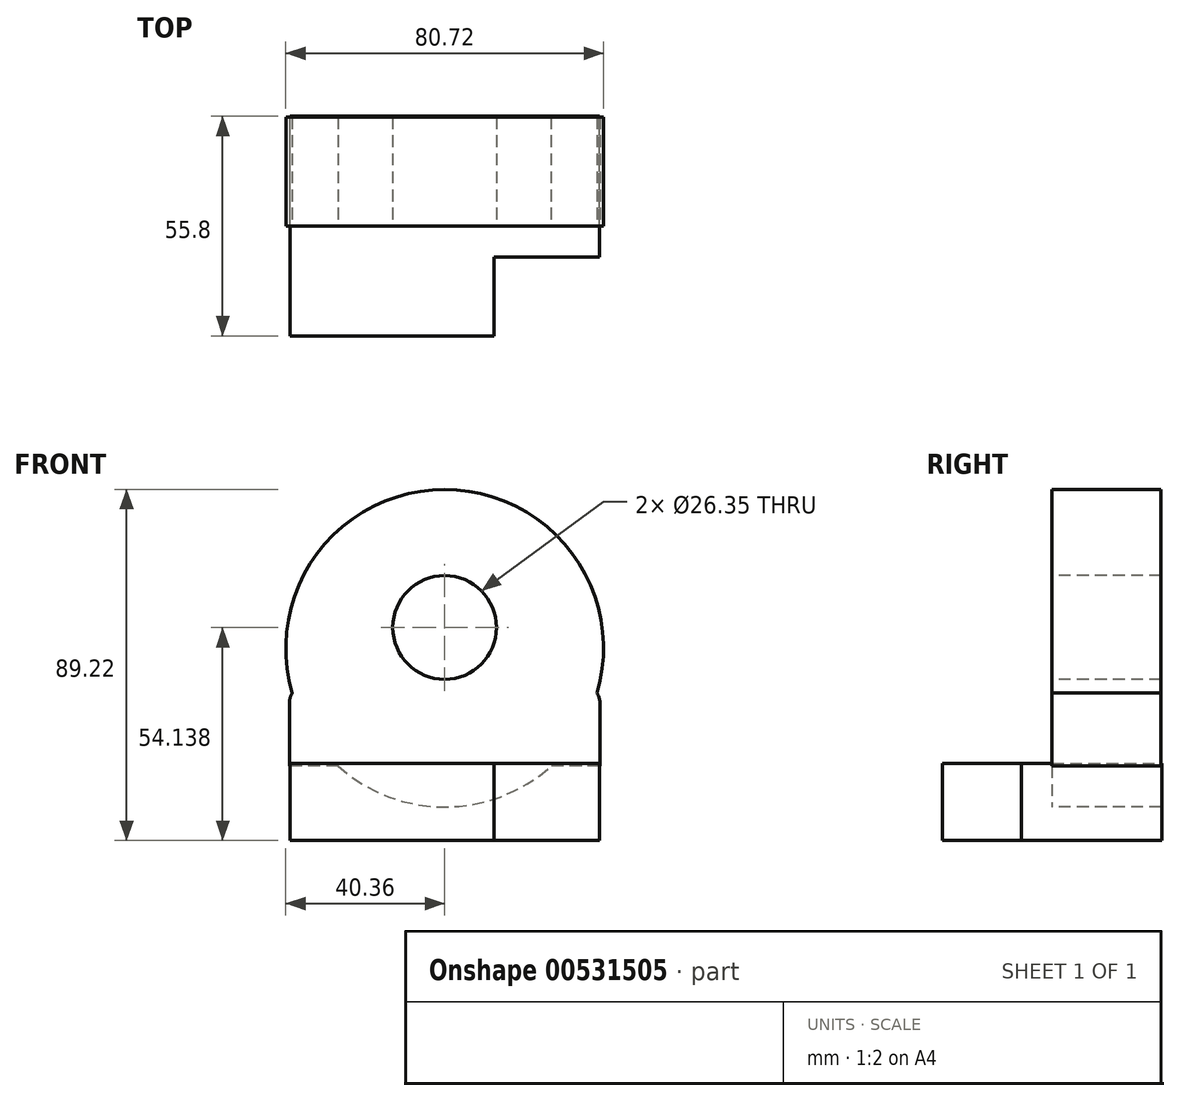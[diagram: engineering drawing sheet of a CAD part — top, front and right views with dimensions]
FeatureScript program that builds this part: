
annotation { "Feature Type Name" : "Feature", "Feature Type Description" : "" }
export const myFeature = defineFeature(function(context is Context, id is Id, definition is map)
    precondition{}
    {
        {
            var Q0;
            Q0=qCreatedBy(makeId("Top.planeOp"),FACE);
            var sketch = newSketch(context, id + "F0", { "sketchPlane" : qUnion([Q0])});
            skLineSegment(sketch, "E0.bottom", {"start": v(-39.31, -27.9) * mm, "end": v(39.31, -27.9) * mm});
            skLineSegment(sketch, "E0.top", {"start": v(-39.31, 27.9) * mm, "end": v(39.31, 27.9) * mm});
            skLineSegment(sketch, "E0.left", {"start": v(-39.31, -27.9) * mm, "end": v(-39.31, 27.9) * mm});
            skLineSegment(sketch, "E0.right", {"start": v(39.31, -27.9) * mm, "end": v(39.31, 27.9) * mm});
            skPoint(sketch, "E0.middle", {"position": v(0, 0) * mm});
            skSolve(sketch);
        }
        {
            var Q0;
            Q0=makeQuery(id+"F0.imprint","IMPRINT",FACE,{"disambiguationData":[TD([[makeQuery(id+"F0.imprint","IMPRINT",EDGE,{"derivedFrom":sQuery(id+"F0.wireOp",EDGE,"E0.bottom")}),1.0]])]});
            extrude(context, id + "F1", {"entities" : qUnion([Q0]), "depth" : 19.56 * mm, "offsetDistance" : 25.4 * mm});
        }
        {
            var Q0;
            Q0=qCreatedBy(makeId("Top.planeOp"),FACE);
            var sketch = newSketch(context, id + "F2", { "sketchPlane" : qUnion([Q0])});
            skLineSegment(sketch, "E1.bottom", {"start": v(39.62, -28.21) * mm, "end": v(12.49, -28.21) * mm});
            skLineSegment(sketch, "E1.top", {"start": v(39.62, -7.86) * mm, "end": v(12.49, -7.86) * mm});
            skLineSegment(sketch, "E1.left", {"start": v(39.62, -28.21) * mm, "end": v(39.62, -7.86) * mm});
            skLineSegment(sketch, "E1.right", {"start": v(12.49, -28.21) * mm, "end": v(12.49, -7.86) * mm});
            skPoint(sketch, "E1.middle", {"position": v(26.05, -18.04) * mm});
            skSolve(sketch);
        }
        {
            var Q0;
            Q0=makeQuery(id+"F2.imprint","IMPRINT",FACE,{"disambiguationData":[TD([[makeQuery(id+"F2.imprint","IMPRINT",EDGE,{"derivedFrom":sQuery(id+"F2.wireOp",EDGE,"E1.bottom")}),-1.0]])]});
            extrude(context, id + "F3", {"entities" : qUnion([Q0]), "operationType" : NewBodyOperationType.REMOVE, "depth" : 29.2 * mm, "offsetDistance" : 25.4 * mm});
        }
        {
            var Q0;
            Q0=qCreatedBy(makeId("Front.planeOp"),FACE);
            var sketch = newSketch(context, id + "F4", { "sketchPlane" : qUnion([Q0])});
            skCircle(sketch, "E2", {"center": v(0, 48.87) * mm, "radius": 40.36 * mm});
            skLineSegment(sketch, "E3.bottom", {"start": v(39.45, 18.93) * mm, "end": v(-39.45, 18.93) * mm});
            skLineSegment(sketch, "E3.top", {"start": v(39.45, 37.47) * mm, "end": v(-39.45, 37.47) * mm});
            skLineSegment(sketch, "E3.left", {"start": v(39.45, 18.93) * mm, "end": v(39.45, 37.47) * mm});
            skLineSegment(sketch, "E3.right", {"start": v(-39.45, 18.93) * mm, "end": v(-39.45, 37.47) * mm});
            skPoint(sketch, "E3.middle", {"position": v(0, 28.2) * mm});
            skSolve(sketch);
        }
        {
            var Q0;
            {var subQ5=sQuery(id+"F4.wireOp",EDGE,"E3.right");Q0=makeQuery(id+"F4.imprint","IMPRINT",FACE,{"disambiguationData":[TD([[makeQuery(id+"F4.imprint","IMPRINT",EDGE,{"derivedFrom":subQ5}),-1.0]])]});}
            var Q1;
            {var subQ0=sQuery(id+"F4.wireOp",EDGE,"E3.bottom");var subQ1=sQuery(id+"F4.wireOp",EDGE,"E2");var subQ2=makeQuery(id+"F4.imprint","INTERSECT",VERTEX,{"disambiguationData":[OD(0.0)],"derivedFrom":[subQ1,subQ0]});Q1=makeQuery(id+"F4.imprint","IMPRINT",FACE,{"disambiguationData":[TD([[makeQuery(id+"F4.imprint","IMPRINT",EDGE,{"disambiguationData":[TD([[subQ2,1.0]])],"derivedFrom":subQ1}),1.0]])]});}
            var Q2;
            {var subQ0=sQuery(id+"F4.wireOp",EDGE,"E3.top");var subQ1=sQuery(id+"F4.wireOp",EDGE,"E2");var subQ2=makeQuery(id+"F4.imprint","INTERSECT",VERTEX,{"disambiguationData":[OD(0.0)],"derivedFrom":[subQ1,subQ0]});Q2=makeQuery(id+"F4.imprint","IMPRINT",FACE,{"disambiguationData":[TD([[makeQuery(id+"F4.imprint","IMPRINT",EDGE,{"disambiguationData":[TD([[subQ2,1.0]])],"derivedFrom":subQ1}),1.0]])]});}
            var Q3;
            {var subQ5=sQuery(id+"F4.wireOp",EDGE,"E3.left");Q3=makeQuery(id+"F4.imprint","IMPRINT",FACE,{"disambiguationData":[TD([[makeQuery(id+"F4.imprint","IMPRINT",EDGE,{"derivedFrom":subQ5}),1.0]])]});}
            var Q4;
            {var subQ0=sQuery(id+"F4.wireOp",EDGE,"E3.top");var subQ1=sQuery(id+"F4.wireOp",EDGE,"E2");var subQ2=makeQuery(id+"F4.imprint","INTERSECT",VERTEX,{"disambiguationData":[OD(0.0)],"derivedFrom":[subQ1,subQ0]});Q4=makeQuery(id+"F4.imprint","IMPRINT",FACE,{"disambiguationData":[TD([[makeQuery(id+"F4.imprint","IMPRINT",EDGE,{"disambiguationData":[TD([[subQ2,-1.0]])],"derivedFrom":subQ1}),1.0]])]});}
            extrude(context, id + "F5", {"entities" : qUnion([Q0, Q1, Q2, Q3, Q4]), "oppositeDirection" : true, "depth" : 27.7 * mm, "offsetDistance" : 25.4 * mm});
        }
        {
            var Q0;
            Q0=makeQuery(id+"F5.opExtrude","CAP_FACE",FACE,{"disambiguationData":[OSD([sQuery(id+"F4.wireOp",EDGE,"E2"),sQuery(id+"F4.wireOp",EDGE,"E3.bottom"),sQuery(id+"F4.wireOp",EDGE,"E3.top"),sQuery(id+"F4.wireOp",EDGE,"E3.left"),sQuery(id+"F4.wireOp",EDGE,"E3.right")])],"isStart":true});
            var sketch = newSketch(context, id + "F6", { "sketchPlane" : qUnion([Q0])});
            skCircle(sketch, "E4", {"center": v(0, 54.14) * mm, "radius": 13.18 * mm});
            skSolve(sketch);
        }
        {
            var Q0;
            Q0=makeQuery(id+"F6.imprint","IMPRINT",FACE,{"disambiguationData":[TD([[makeQuery(id+"F6.imprint","IMPRINT",EDGE,{"derivedFrom":sQuery(id+"F6.wireOp",EDGE,"E4")}),1.0]])]});
            extrude(context, id + "F7", {"entities" : qUnion([Q0]), "operationType" : NewBodyOperationType.REMOVE, "oppositeDirection" : true, "depth" : 29.2 * mm, "offsetDistance" : 25.4 * mm});
        }
        {
            var Q0;
            Q0=makeQuery(id+"F5.opExtrude","SWEPT_EDGE",EDGE,{"disambiguationData":[OSD([sQuery(id+"F4.wireOp",EDGE,"E3.top"),sQuery(id+"F4.wireOp",EDGE,"E3.right")])]});
            var Q1;
            Q1=makeQuery(id+"F5.opExtrude","SWEPT_EDGE",EDGE,{"disambiguationData":[OSD([sQuery(id+"F4.wireOp",EDGE,"E3.top"),sQuery(id+"F4.wireOp",EDGE,"E3.left")])]});
            fillet(context, id + "F8", {"entities" : qUnion([Q0, Q1]), "radius" : 5.08 * mm, "tangentPropagation" : true, "allowEdgeOverflow" : false});
        }
    });
